# Revit family: Artek_Stools_Stool 60_Stool 60_configurable_product
name_source: partatom
category: Furniture
revit_build: Autodesk Revit 2017 (Build: 20190508_0315(x64)
units: mm (PartAtom-declared; Revit-internal decimal feet)

## family parameters
Always vertical = Yes
Cut with Voids When Loaded = No
OmniClass Number = 23.40.20.14.14.11
OmniClass Title = Chairs
Room Calculation Point = No
Shared = No
Work Plane-Based = No

## types (1)
- Stool 60 (configurable)
    AssetType = Movable
    BIMObjectName = Furniture_Chairs_Artek_Stool_60
    Brand = Artek
    Category = Stools
    Collection = Stool 60
    Color = Various
    Cost = 0 $
    Description = Alvar Aalto’s iconic Stool 60 is the most elemental of furniture pieces, equally suitable as a seat, a table, storage unit, or display surface. The legs are mounted directly to the underside of the round seat without the need for complicated connecting elements. Thanks to its geometry, the stool can be stacked to save space in a spiralling tower sculpture. Manufactured in 42 production steps at the A-Factory in Turku, Finland, Stool 60 is available in a wide variety of colours and finishes. Several million units of Stool 60 and its four-legged cousin, Stool E60, have been sold, making it one of the most cherished products in the history of design.
    Designer = Alvar Aalto
    DurationUnit = Years
    Features = Stool 60 can be stacked to create a spiralling tower of design classics Made of solid birch in Finland The simple geometry of Stool 60 has an elemental power
    Finish = Three legs and seat edge-band:
Solid birch
Seat core versions:
Solid birch, Birch plywood
Seat surface versions:
Birch veneer, High-pressure laminate, Linoleum, Fabric upholstery and PU foam padding, Leather upholstery and PU foam padding, Leather upholstery
    IfcExportAs = IfcFurnishingElementType
    IfcExportType = CHAIR
    MainColor = Various
    Manufacturer = Artek
    ManufacturerName = Artek
    ManufacturerURL = https://www.artek.fi
    Material = Wood/Fabric/Textile
    Model = Stool 60
    ModelNumber = 280001*
    NBSDescription = Domestic chairs
    NBSReference = 45-35-20/365
    Name = Stool_60
    NominalDepth = 380 mm
    NominalHeight = 440 mm  [stored 1.44357 ft]
    NominalLength = 380 mm
    ProductInformation = Alvar Aalto’s iconic Stool 60 is the most elemental of furniture pieces, equally suitable as a seat, a table, storage unit, or display surface. The legs are mounted directly to the underside of the round seat without the need for complicated connecting elements. Thanks to its geometry, the stool can be stacked to save space in a spiralling tower sculpture. Manufactured in 42 production steps at the A-Factory in Turku, Finland, Stool 60 is available in a wide variety of colours and finishes. Several million units of Stool 60 and its four-legged cousin, Stool E60, have been sold, making it one of the most cherished products in the history of design.
    Revision = 1
    SeatingHeight = 440 mm  [stored 1.44357 ft]
    Shape = Sculptured
    Size = 380x380x440mm
    URL = https://www.artek.fi
    Uniclass2 = Pr_40_50_12_83
    Uniclass2015Description = Foot stools
    Uniclass2015Reference = Pr_40_50_51_31
    Version = 1
    VersionDate = 12/11/2020

note: [stored X ft] marks values corroborated as IEEE doubles in the binary element streams (Revit-internal decimal feet)

## geometry (parser evidence)
native form markers: Sweep x2
no freeform markers — native parametric forms only
